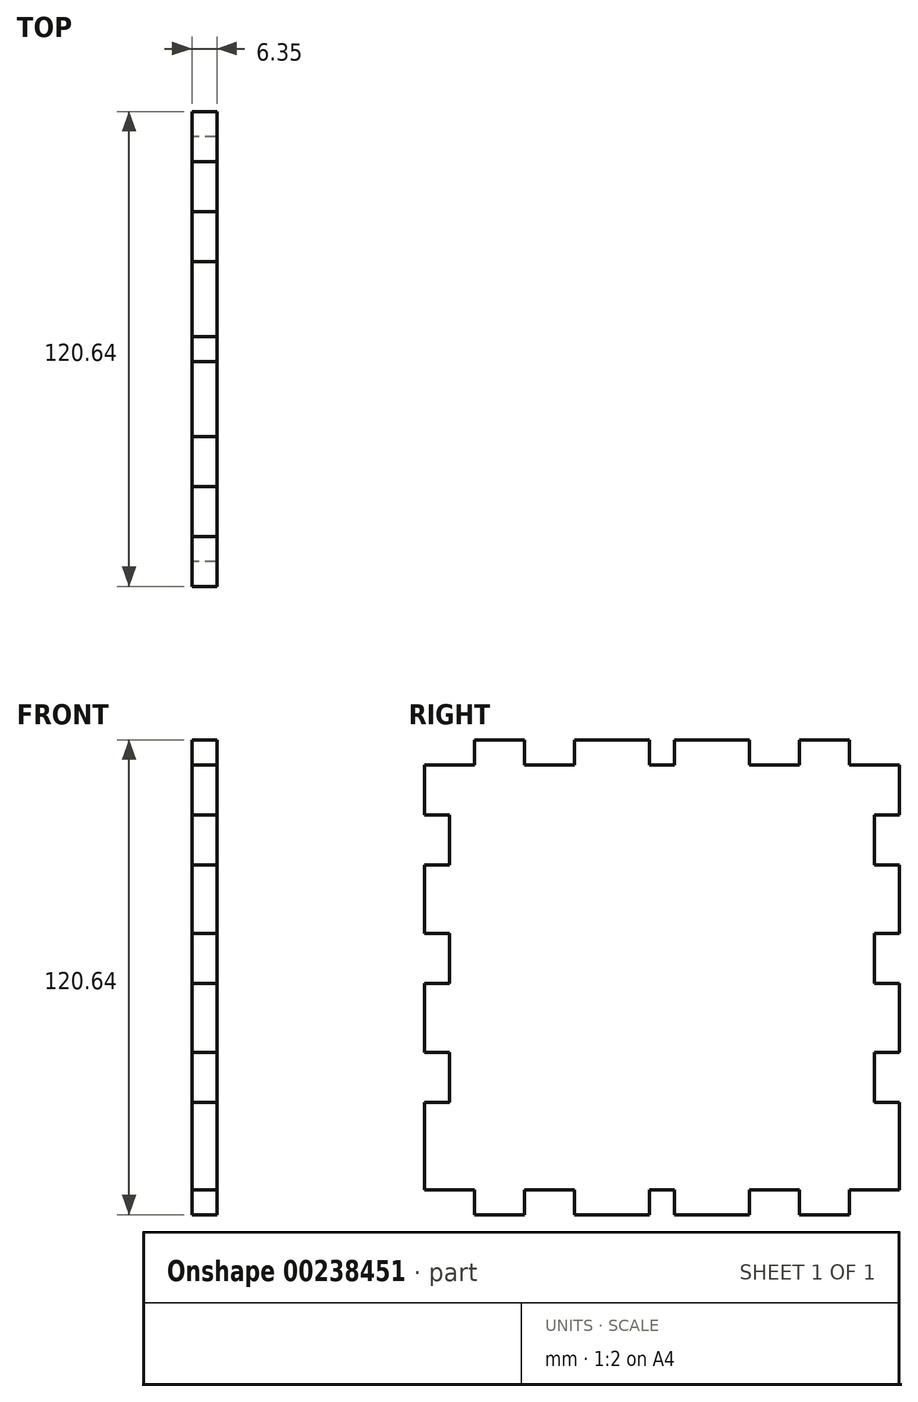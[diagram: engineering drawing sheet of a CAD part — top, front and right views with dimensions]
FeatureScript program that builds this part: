
annotation { "Feature Type Name" : "Feature", "Feature Type Description" : "" }
export const myFeature = defineFeature(function(context is Context, id is Id, definition is map)
    precondition{}
    {
        {
            var Q0;
            Q0=qCreatedBy(makeId("Right.planeOp"),FACE);
            var sketch = newSketch(context, id + "F0", { "sketchPlane" : qUnion([Q0])});
            skLineSegment(sketch, "E0.bottom", {"start": v(60.32, 60.33) * mm, "end": v(-60.33, 60.33) * mm});
            skLineSegment(sketch, "E0.top", {"start": v(60.33, -60.33) * mm, "end": v(-60.32, -60.33) * mm});
            skLineSegment(sketch, "E0.left", {"start": v(60.32, 60.33) * mm, "end": v(60.33, -60.33) * mm});
            skLineSegment(sketch, "E0.right", {"start": v(-60.33, 60.33) * mm, "end": v(-60.32, -60.33) * mm});
            skPoint(sketch, "E0.middle", {"position": v(0, 0) * mm});
            skSolve(sketch);
        }
        {
            var Q0;
            Q0=makeQuery(id+"F0.imprint","IMPRINT",FACE,{"disambiguationData":[TD([[makeQuery(id+"F0.imprint","IMPRINT",EDGE,{"derivedFrom":sQuery(id+"F0.wireOp",EDGE,"E0.bottom")}),1.0]])]});
            extrude(context, id + "F1", {"entities" : qUnion([Q0]), "depth" : 6.35 * mm});
        }
        {
            var Q0;
            Q0=makeQuery(id+"F1.opExtrude","CAP_FACE",FACE,{"disambiguationData":[OSD([sQuery(id+"F0.wireOp",EDGE,"E0.bottom"),sQuery(id+"F0.wireOp",EDGE,"E0.top"),sQuery(id+"F0.wireOp",EDGE,"E0.left"),sQuery(id+"F0.wireOp",EDGE,"E0.right")])],"isStart":true});
            var sketch = newSketch(context, id + "F2", { "sketchPlane" : qUnion([Q0])});
            skLineSegment(sketch, "E1.bottom", {"start": v(60.33, 60.33) * mm, "end": v(47.63, 60.33) * mm});
            skLineSegment(sketch, "E1.top", {"start": v(60.33, 53.98) * mm, "end": v(47.63, 53.98) * mm});
            skLineSegment(sketch, "E1.left", {"start": v(60.33, 60.33) * mm, "end": v(60.33, 53.98) * mm});
            skLineSegment(sketch, "E1.right", {"start": v(47.63, 60.33) * mm, "end": v(47.63, 53.98) * mm});
            skSolve(sketch);
        }
        {
            var Q0;
            Q0=makeQuery(id+"F2.imprint","IMPRINT",FACE,{"disambiguationData":[TD([[makeQuery(id+"F2.imprint","IMPRINT",EDGE,{"derivedFrom":sQuery(id+"F2.wireOp",EDGE,"E1.bottom")}),-1.0]])]});
            extrude(context, id + "F3", {"entities" : qUnion([Q0]), "operationType" : NewBodyOperationType.REMOVE, "endBound" : BoundingType.THROUGH_ALL, "oppositeDirection" : true, "depth" : 1.59 * mm});
        }
        {
            var Q0;
            Q0=makeQuery(id+"F1.opExtrude","CAP_FACE",FACE,{"disambiguationData":[OSD([sQuery(id+"F0.wireOp",EDGE,"E0.bottom"),sQuery(id+"F0.wireOp",EDGE,"E0.top"),sQuery(id+"F0.wireOp",EDGE,"E0.left"),sQuery(id+"F0.wireOp",EDGE,"E0.right")])],"isStart":true});
            var sketch = newSketch(context, id + "F4", { "sketchPlane" : qUnion([Q0])});
            skLineSegment(sketch, "E2.bottom", {"start": v(34.93, 60.33) * mm, "end": v(22.23, 60.33) * mm});
            skLineSegment(sketch, "E2.top", {"start": v(34.93, 53.98) * mm, "end": v(22.23, 53.98) * mm});
            skLineSegment(sketch, "E2.left", {"start": v(34.93, 60.33) * mm, "end": v(34.93, 53.98) * mm});
            skLineSegment(sketch, "E2.right", {"start": v(22.23, 60.33) * mm, "end": v(22.23, 53.98) * mm});
            skSolve(sketch);
        }
        {
            var Q0;
            Q0 = qSketchRegion(id + "F4", true);
            extrude(context, id + "F5", {"entities" : qUnion([Q0]), "operationType" : NewBodyOperationType.REMOVE, "endBound" : BoundingType.THROUGH_ALL, "oppositeDirection" : true, "depth" : 1.59 * mm});
        }
        {
            var Q0;
            Q0=makeQuery(id+"F1.opExtrude","CAP_FACE",FACE,{"disambiguationData":[OSD([sQuery(id+"F0.wireOp",EDGE,"E0.bottom"),sQuery(id+"F0.wireOp",EDGE,"E0.top"),sQuery(id+"F0.wireOp",EDGE,"E0.left"),sQuery(id+"F0.wireOp",EDGE,"E0.right")])],"isStart":true});
            var sketch = newSketch(context, id + "F6", { "sketchPlane" : qUnion([Q0])});
            skLineSegment(sketch, "E3.bottom", {"start": v(3.18, 60.33) * mm, "end": v(-3.17, 60.33) * mm});
            skLineSegment(sketch, "E3.top", {"start": v(3.18, 53.98) * mm, "end": v(-3.17, 53.98) * mm});
            skLineSegment(sketch, "E3.left", {"start": v(3.18, 60.33) * mm, "end": v(3.18, 53.98) * mm});
            skLineSegment(sketch, "E3.right", {"start": v(-3.17, 60.33) * mm, "end": v(-3.17, 53.98) * mm});
            skSolve(sketch);
        }
        {
            var Q0;
            Q0 = qSketchRegion(id + "F6", true);
            extrude(context, id + "F7", {"entities" : qUnion([Q0]), "operationType" : NewBodyOperationType.REMOVE, "endBound" : BoundingType.THROUGH_ALL, "oppositeDirection" : true, "depth" : 1.59 * mm});
        }
        {
            var Q0;
            Q0=makeQuery(id+"F1.opExtrude","CAP_FACE",FACE,{"disambiguationData":[OSD([sQuery(id+"F0.wireOp",EDGE,"E0.bottom"),sQuery(id+"F0.wireOp",EDGE,"E0.top"),sQuery(id+"F0.wireOp",EDGE,"E0.left"),sQuery(id+"F0.wireOp",EDGE,"E0.right")])],"isStart":true});
            var sketch = newSketch(context, id + "F8", { "sketchPlane" : qUnion([Q0])});
            skLineSegment(sketch, "E4.bottom", {"start": v(-60.32, 60.33) * mm, "end": v(-47.62, 60.33) * mm});
            skLineSegment(sketch, "E4.top", {"start": v(-60.32, 53.98) * mm, "end": v(-47.62, 53.98) * mm});
            skLineSegment(sketch, "E4.left", {"start": v(-60.32, 60.33) * mm, "end": v(-60.32, 53.98) * mm});
            skLineSegment(sketch, "E4.right", {"start": v(-47.62, 60.33) * mm, "end": v(-47.62, 53.98) * mm});
            skSolve(sketch);
        }
        {
            var Q0;
            Q0=makeQuery(id+"F8.imprint","IMPRINT",FACE,{"disambiguationData":[TD([[makeQuery(id+"F8.imprint","IMPRINT",EDGE,{"derivedFrom":sQuery(id+"F8.wireOp",EDGE,"E4.bottom")}),-1.0]])]});
            extrude(context, id + "F9", {"entities" : qUnion([Q0]), "operationType" : NewBodyOperationType.REMOVE, "endBound" : BoundingType.THROUGH_ALL, "oppositeDirection" : true, "depth" : 1.59 * mm});
        }
        {
            var Q0;
            Q0=makeQuery(id+"F1.opExtrude","CAP_FACE",FACE,{"disambiguationData":[OSD([sQuery(id+"F0.wireOp",EDGE,"E0.bottom"),sQuery(id+"F0.wireOp",EDGE,"E0.top"),sQuery(id+"F0.wireOp",EDGE,"E0.left"),sQuery(id+"F0.wireOp",EDGE,"E0.right")])],"isStart":true});
            var sketch = newSketch(context, id + "F10", { "sketchPlane" : qUnion([Q0])});
            skLineSegment(sketch, "E5.bottom", {"start": v(-22.22, 60.33) * mm, "end": v(-34.92, 60.33) * mm});
            skLineSegment(sketch, "E5.top", {"start": v(-22.22, 53.98) * mm, "end": v(-34.92, 53.98) * mm});
            skLineSegment(sketch, "E5.left", {"start": v(-22.22, 60.33) * mm, "end": v(-22.22, 53.98) * mm});
            skLineSegment(sketch, "E5.right", {"start": v(-34.92, 60.33) * mm, "end": v(-34.92, 53.98) * mm});
            skSolve(sketch);
        }
        {
            var Q0;
            Q0=makeQuery(id+"F10.imprint","IMPRINT",FACE,{"disambiguationData":[TD([[makeQuery(id+"F10.imprint","IMPRINT",EDGE,{"derivedFrom":sQuery(id+"F10.wireOp",EDGE,"E5.bottom")}),-1.0]])]});
            extrude(context, id + "F11", {"entities" : qUnion([Q0]), "operationType" : NewBodyOperationType.REMOVE, "endBound" : BoundingType.THROUGH_ALL, "oppositeDirection" : true, "depth" : 1.59 * mm});
        }
        {
            var Q0;
            Q0=makeQuery(id+"F1.opExtrude","CAP_FACE",FACE,{"disambiguationData":[OSD([sQuery(id+"F0.wireOp",EDGE,"E0.bottom"),sQuery(id+"F0.wireOp",EDGE,"E0.top"),sQuery(id+"F0.wireOp",EDGE,"E0.left"),sQuery(id+"F0.wireOp",EDGE,"E0.right")])],"isStart":true});
            var sketch = newSketch(context, id + "F12", { "sketchPlane" : qUnion([Q0])});
            skLineSegment(sketch, "E6.bottom", {"start": v(-60.32, 41.28) * mm, "end": v(-53.97, 41.28) * mm});
            skLineSegment(sketch, "E6.top", {"start": v(-60.32, 28.58) * mm, "end": v(-53.97, 28.58) * mm});
            skLineSegment(sketch, "E6.left", {"start": v(-60.32, 41.28) * mm, "end": v(-60.32, 28.57) * mm});
            skLineSegment(sketch, "E6.right", {"start": v(-53.97, 41.28) * mm, "end": v(-53.97, 28.58) * mm});
            skSolve(sketch);
        }
        {
            var Q0;
            Q0=makeQuery(id+"F12.imprint","IMPRINT",FACE,{"disambiguationData":[TD([[makeQuery(id+"F12.imprint","IMPRINT",EDGE,{"derivedFrom":sQuery(id+"F12.wireOp",EDGE,"E6.bottom")}),-1.0]])]});
            extrude(context, id + "F13", {"entities" : qUnion([Q0]), "operationType" : NewBodyOperationType.REMOVE, "endBound" : BoundingType.THROUGH_ALL, "oppositeDirection" : true, "depth" : 1.59 * mm});
        }
        {
            var Q0;
            Q0=makeQuery(id+"F1.opExtrude","CAP_FACE",FACE,{"disambiguationData":[OSD([sQuery(id+"F0.wireOp",EDGE,"E0.bottom"),sQuery(id+"F0.wireOp",EDGE,"E0.top"),sQuery(id+"F0.wireOp",EDGE,"E0.left"),sQuery(id+"F0.wireOp",EDGE,"E0.right")])],"isStart":true});
            var sketch = newSketch(context, id + "F14", { "sketchPlane" : qUnion([Q0])});
            skLineSegment(sketch, "E7.bottom", {"start": v(-60.32, 11.11) * mm, "end": v(-53.97, 11.11) * mm});
            skLineSegment(sketch, "E7.top", {"start": v(-60.32, -1.59) * mm, "end": v(-53.97, -1.59) * mm});
            skLineSegment(sketch, "E7.left", {"start": v(-60.32, 11.11) * mm, "end": v(-60.32, -1.59) * mm});
            skLineSegment(sketch, "E7.right", {"start": v(-53.97, 11.11) * mm, "end": v(-53.97, -1.59) * mm});
            skSolve(sketch);
        }
        {
            var Q0;
            Q0=makeQuery(id+"F14.imprint","IMPRINT",FACE,{"disambiguationData":[TD([[makeQuery(id+"F14.imprint","IMPRINT",EDGE,{"derivedFrom":sQuery(id+"F14.wireOp",EDGE,"E7.bottom")}),-1.0]])]});
            extrude(context, id + "F15", {"entities" : qUnion([Q0]), "operationType" : NewBodyOperationType.REMOVE, "endBound" : BoundingType.THROUGH_ALL, "oppositeDirection" : true, "depth" : 1.59 * mm});
        }
        {
            var Q0;
            Q0=makeQuery(id+"F1.opExtrude","CAP_FACE",FACE,{"disambiguationData":[OSD([sQuery(id+"F0.wireOp",EDGE,"E0.bottom"),sQuery(id+"F0.wireOp",EDGE,"E0.top"),sQuery(id+"F0.wireOp",EDGE,"E0.left"),sQuery(id+"F0.wireOp",EDGE,"E0.right")])],"isStart":true});
            var sketch = newSketch(context, id + "F16", { "sketchPlane" : qUnion([Q0])});
            skLineSegment(sketch, "E8.bottom", {"start": v(-60.33, -19.05) * mm, "end": v(-53.98, -19.05) * mm});
            skLineSegment(sketch, "E8.top", {"start": v(-60.33, -31.75) * mm, "end": v(-53.98, -31.75) * mm});
            skLineSegment(sketch, "E8.left", {"start": v(-60.33, -19.05) * mm, "end": v(-60.33, -31.75) * mm});
            skLineSegment(sketch, "E8.right", {"start": v(-53.98, -19.05) * mm, "end": v(-53.98, -31.75) * mm});
            skSolve(sketch);
        }
        {
            var Q0;
            Q0=makeQuery(id+"F16.imprint","IMPRINT",FACE,{"disambiguationData":[TD([[makeQuery(id+"F16.imprint","IMPRINT",EDGE,{"derivedFrom":sQuery(id+"F16.wireOp",EDGE,"E8.bottom")}),-1.0]])]});
            extrude(context, id + "F17", {"entities" : qUnion([Q0]), "operationType" : NewBodyOperationType.REMOVE, "endBound" : BoundingType.THROUGH_ALL, "oppositeDirection" : true, "depth" : 1.59 * mm});
        }
        {
            var Q0;
            Q0=makeQuery(id+"F1.opExtrude","CAP_FACE",FACE,{"disambiguationData":[OSD([sQuery(id+"F0.wireOp",EDGE,"E0.bottom"),sQuery(id+"F0.wireOp",EDGE,"E0.top"),sQuery(id+"F0.wireOp",EDGE,"E0.left"),sQuery(id+"F0.wireOp",EDGE,"E0.right")])],"isStart":true});
            var sketch = newSketch(context, id + "F18", { "sketchPlane" : qUnion([Q0])});
            skLineSegment(sketch, "E9.bottom", {"start": v(-60.33, -53.98) * mm, "end": v(-47.63, -53.98) * mm});
            skLineSegment(sketch, "E9.top", {"start": v(-60.33, -60.33) * mm, "end": v(-47.63, -60.33) * mm});
            skLineSegment(sketch, "E9.left", {"start": v(-60.33, -53.98) * mm, "end": v(-60.33, -60.33) * mm});
            skLineSegment(sketch, "E9.right", {"start": v(-47.63, -53.98) * mm, "end": v(-47.63, -60.33) * mm});
            skLineSegment(sketch, "E10.bottom", {"start": v(60.32, -53.98) * mm, "end": v(47.62, -53.98) * mm});
            skLineSegment(sketch, "E10.top", {"start": v(60.32, -60.33) * mm, "end": v(47.62, -60.33) * mm});
            skLineSegment(sketch, "E10.left", {"start": v(60.32, -53.98) * mm, "end": v(60.32, -60.33) * mm});
            skLineSegment(sketch, "E10.right", {"start": v(47.62, -53.98) * mm, "end": v(47.62, -60.33) * mm});
            skSolve(sketch);
        }
        {
            var Q0;
            Q0 = qSketchRegion(id + "F18", true);
            extrude(context, id + "F19", {"entities" : qUnion([Q0]), "operationType" : NewBodyOperationType.REMOVE, "endBound" : BoundingType.THROUGH_ALL, "oppositeDirection" : true, "depth" : 1.59 * mm});
        }
        {
            var Q0;
            Q0=makeQuery(id+"F1.opExtrude","CAP_FACE",FACE,{"disambiguationData":[OSD([sQuery(id+"F0.wireOp",EDGE,"E0.bottom"),sQuery(id+"F0.wireOp",EDGE,"E0.top"),sQuery(id+"F0.wireOp",EDGE,"E0.left"),sQuery(id+"F0.wireOp",EDGE,"E0.right")])],"isStart":true});
            var sketch = newSketch(context, id + "F20", { "sketchPlane" : qUnion([Q0])});
            skLineSegment(sketch, "E11.bottom", {"start": v(-34.93, -60.33) * mm, "end": v(-22.23, -60.33) * mm});
            skLineSegment(sketch, "E11.top", {"start": v(-34.93, -53.98) * mm, "end": v(-22.23, -53.98) * mm});
            skLineSegment(sketch, "E11.left", {"start": v(-34.93, -60.33) * mm, "end": v(-34.93, -53.98) * mm});
            skLineSegment(sketch, "E11.right", {"start": v(-22.23, -60.33) * mm, "end": v(-22.23, -53.98) * mm});
            skLineSegment(sketch, "E12.bottom", {"start": v(-3.18, -60.33) * mm, "end": v(3.17, -60.33) * mm});
            skLineSegment(sketch, "E12.top", {"start": v(-3.18, -53.98) * mm, "end": v(3.17, -53.98) * mm});
            skLineSegment(sketch, "E12.left", {"start": v(-3.18, -60.33) * mm, "end": v(-3.18, -53.98) * mm});
            skLineSegment(sketch, "E12.right", {"start": v(3.17, -60.33) * mm, "end": v(3.17, -53.98) * mm});
            skLineSegment(sketch, "E13.bottom", {"start": v(22.22, -60.33) * mm, "end": v(34.92, -60.33) * mm});
            skLineSegment(sketch, "E13.top", {"start": v(22.22, -53.97) * mm, "end": v(34.92, -53.97) * mm});
            skLineSegment(sketch, "E13.left", {"start": v(22.22, -60.33) * mm, "end": v(22.22, -53.97) * mm});
            skLineSegment(sketch, "E13.right", {"start": v(34.92, -60.33) * mm, "end": v(34.92, -53.97) * mm});
            skSolve(sketch);
        }
        {
            var Q0;
            Q0 = qSketchRegion(id + "F20", true);
            extrude(context, id + "F21", {"entities" : qUnion([Q0]), "operationType" : NewBodyOperationType.REMOVE, "endBound" : BoundingType.THROUGH_ALL, "oppositeDirection" : true, "depth" : 1.59 * mm});
        }
        {
            var Q0;
            Q0=makeQuery(id+"F1.opExtrude","CAP_FACE",FACE,{"disambiguationData":[OSD([sQuery(id+"F0.wireOp",EDGE,"E0.bottom"),sQuery(id+"F0.wireOp",EDGE,"E0.top"),sQuery(id+"F0.wireOp",EDGE,"E0.left"),sQuery(id+"F0.wireOp",EDGE,"E0.right")])],"isStart":true});
            var sketch = newSketch(context, id + "F22", { "sketchPlane" : qUnion([Q0])});
            skLineSegment(sketch, "E14.bottom", {"start": v(60.33, 41.27) * mm, "end": v(53.98, 41.27) * mm});
            skLineSegment(sketch, "E14.top", {"start": v(60.33, 28.57) * mm, "end": v(53.98, 28.57) * mm});
            skLineSegment(sketch, "E14.left", {"start": v(60.33, 41.27) * mm, "end": v(60.33, 28.57) * mm});
            skLineSegment(sketch, "E14.right", {"start": v(53.98, 41.27) * mm, "end": v(53.98, 28.57) * mm});
            skLineSegment(sketch, "E15.bottom", {"start": v(60.33, 11.11) * mm, "end": v(53.98, 11.11) * mm});
            skLineSegment(sketch, "E15.top", {"start": v(60.33, -1.59) * mm, "end": v(53.98, -1.59) * mm});
            skLineSegment(sketch, "E15.left", {"start": v(60.33, 11.11) * mm, "end": v(60.33, -1.59) * mm});
            skLineSegment(sketch, "E15.right", {"start": v(53.98, 11.11) * mm, "end": v(53.98, -1.59) * mm});
            skSolve(sketch);
        }
        {
            var Q0;
            Q0 = qSketchRegion(id + "F22", true);
            extrude(context, id + "F23", {"entities" : qUnion([Q0]), "operationType" : NewBodyOperationType.REMOVE, "endBound" : BoundingType.THROUGH_ALL, "oppositeDirection" : true, "depth" : 1.59 * mm});
        }
        {
            var Q0;
            Q0=makeQuery(id+"F1.opExtrude","CAP_FACE",FACE,{"disambiguationData":[OSD([sQuery(id+"F0.wireOp",EDGE,"E0.bottom"),sQuery(id+"F0.wireOp",EDGE,"E0.top"),sQuery(id+"F0.wireOp",EDGE,"E0.left"),sQuery(id+"F0.wireOp",EDGE,"E0.right")])],"isStart":true});
            var sketch = newSketch(context, id + "F24", { "sketchPlane" : qUnion([Q0])});
            skLineSegment(sketch, "E16.bottom", {"start": v(60.33, -19.05) * mm, "end": v(53.98, -19.05) * mm});
            skLineSegment(sketch, "E16.top", {"start": v(60.33, -31.75) * mm, "end": v(53.98, -31.75) * mm});
            skLineSegment(sketch, "E16.left", {"start": v(60.33, -19.05) * mm, "end": v(60.33, -31.75) * mm});
            skLineSegment(sketch, "E16.right", {"start": v(53.98, -19.05) * mm, "end": v(53.98, -31.75) * mm});
            skSolve(sketch);
        }
        {
            var Q0;
            Q0 = qSketchRegion(id + "F24", true);
            extrude(context, id + "F25", {"entities" : qUnion([Q0]), "operationType" : NewBodyOperationType.REMOVE, "endBound" : BoundingType.THROUGH_ALL, "oppositeDirection" : true, "depth" : 1.59 * mm});
        }
    });
